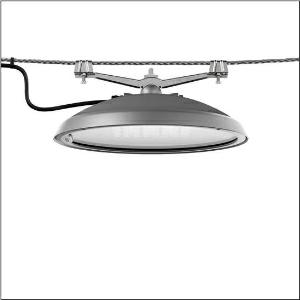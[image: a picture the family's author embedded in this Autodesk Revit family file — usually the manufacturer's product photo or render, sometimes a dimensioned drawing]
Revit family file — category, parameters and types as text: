
# Revit family: dl_r__50_iq_mini___p1_0s_5xa248u31f08fe_9f5a
name_source: partatom
category: Lighting Fixtures
units: mm (PartAtom-declared; Revit-internal decimal feet)

## family parameters
Cut with Voids When Loaded = No
Host = Face
Light Source = No
Part Type = Normal
Room Calculation Point = No
Round Connector Dimension = Use Diameter
Shared = No

## types (1)
- --- (1 x LED, 2610 lm, 16.3 W, 3000K)
    Apparent Load = 16 VA
    CIE Flux Codes = 23 54 93 100 100
    Color Rendering = 70
    Color Temperature = 3000K
    Default Elevation = 1800 mm
    Description = DL® 50 iQ mini, catenary luminaire, primary light control with lens, of PMMA, primary optical cover: cover, of toughened safety glass, transparent, light distribution: P1.0s, light emission: direct distribution, primary light characteristic: symmetric, installation type: suspended mounting, LED, High Power LED, rated luminous flux: 2.610lm, luminous efficacy: 160lm/W, light colour: 730, colour temperature: 3000K, control: optimised constant luminous flux control (CLO 2.0), Desk-Remote (wireless, voltage-free reading and setting of iQ features in the workshop via application-optimized NFC function/RFID function), Light-Fading, Smart-Wire, Night-Set, Lumen-Switch, Temp-Guard, Auto-Match, Street-Remote, mains connection: 230..240V, AC, 50/60Hz, start of lifetime: 16W, end of service life: 17W, reduction: 8W, luminaire housing, of diecast aluminium, powder-coated, Siteco® metallic grey (DB 702S), diameter: 500mm, height: 115mm, protection rating (complete): IP66, insulation class (complete): insulation class II (safety insulation), certification: CE, ENEC, VDE, impact resistance: IK08, permissible operating ambient temperature for outdoor applications: -25..+40°C, standard-compliant lighting for roads and squares, packaging unit: 1 piece

Light Distribution: P1.0s
    Height = 124 mm  [stored 0.406824 ft]
    Lamp = 1 x LED
    Lamp Light Flux = 2610 lm
    Lamp Power = 16.3 W
    Lamp count = 1
    Length = 500 mm
    Luminous efficacy = 160 lm/W
    Manufacturer = Siteco
    ModVariant = No
    Model = 5XA248U31F08FE
    Number of Poles = 1
    OnlyDefault = Yes
    Power Factor = 1
    Product Name = DL® 50 iQ mini | P1.0s
    Product group = catenary luminaire
    ProductGroupID = 6300
    Protection Class = Protection class II
    Protection Degree = IP 66
    RLX_Detail_Level = 1
    RLX_Emergency_Light_Flux = 0 lm
    RLX_Emergency_Type = 0
    RLX_Emergency_Type_DB = No
    RlxData = <blob elided: 122813 chars, md5=696f499e>
    Socket = socket
    Standby Power = 0 W
    System Light Flux = 2610 lm
    System Power = 16 W
    Type Comments = factory setting: luminous flux: 100 % | dim-lin: 254 | 333 mA
    Type Image = l_1242791.jpg
    URL = http://relux.com
    VarID = @adj_069119
    Voltage = 0 V
    Weight = 0.00 kg
    Width = 0 mm  [stored 0 ft]

note: [stored X ft] marks values corroborated as IEEE doubles in the binary element streams (Revit-internal decimal feet)

## geometry (parser evidence)
native form markers: Blend x4, Sweep x11
no freeform markers — native parametric forms only
